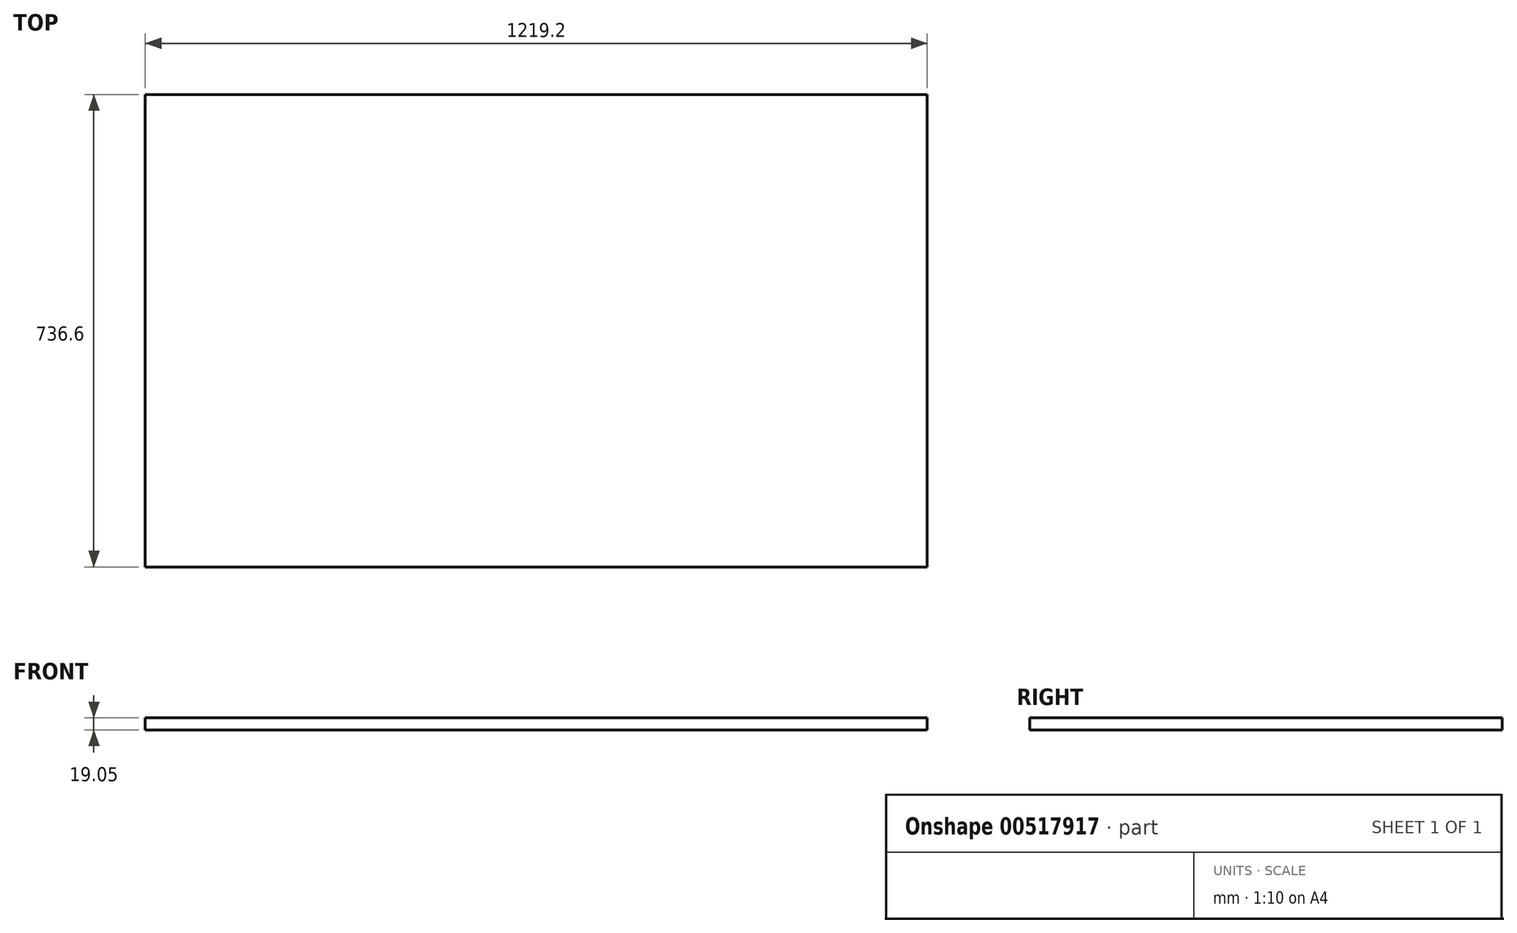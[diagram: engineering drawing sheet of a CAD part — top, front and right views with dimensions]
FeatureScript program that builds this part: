
annotation { "Feature Type Name" : "Feature", "Feature Type Description" : "" }
export const myFeature = defineFeature(function(context is Context, id is Id, definition is map)
    precondition{}
    {
        {
            var Q0;
            Q0=qCreatedBy(makeId("Top.planeOp"),FACE);
            var sketch = newSketch(context, id + "F0", { "sketchPlane" : qUnion([Q0])});
            skLineSegment(sketch, "E0.bottom", {"start": v(609.6, 368.3) * mm, "end": v(-609.6, 368.3) * mm});
            skLineSegment(sketch, "E0.top", {"start": v(609.6, -368.3) * mm, "end": v(-609.6, -368.3) * mm});
            skLineSegment(sketch, "E0.left", {"start": v(609.6, 368.3) * mm, "end": v(609.6, -368.3) * mm});
            skLineSegment(sketch, "E0.right", {"start": v(-609.6, 368.3) * mm, "end": v(-609.6, -368.3) * mm});
            skPoint(sketch, "E0.middle", {"position": v(0, 0) * mm});
            skSolve(sketch);
        }
        {
            var Q0;
            Q0 = qSketchRegion(id + "F0", true);
            extrude(context, id + "F1", {"entities" : qUnion([Q0]), "depth" : 19.05 * mm, "offsetDistance" : 25.4 * mm});
        }
    });
